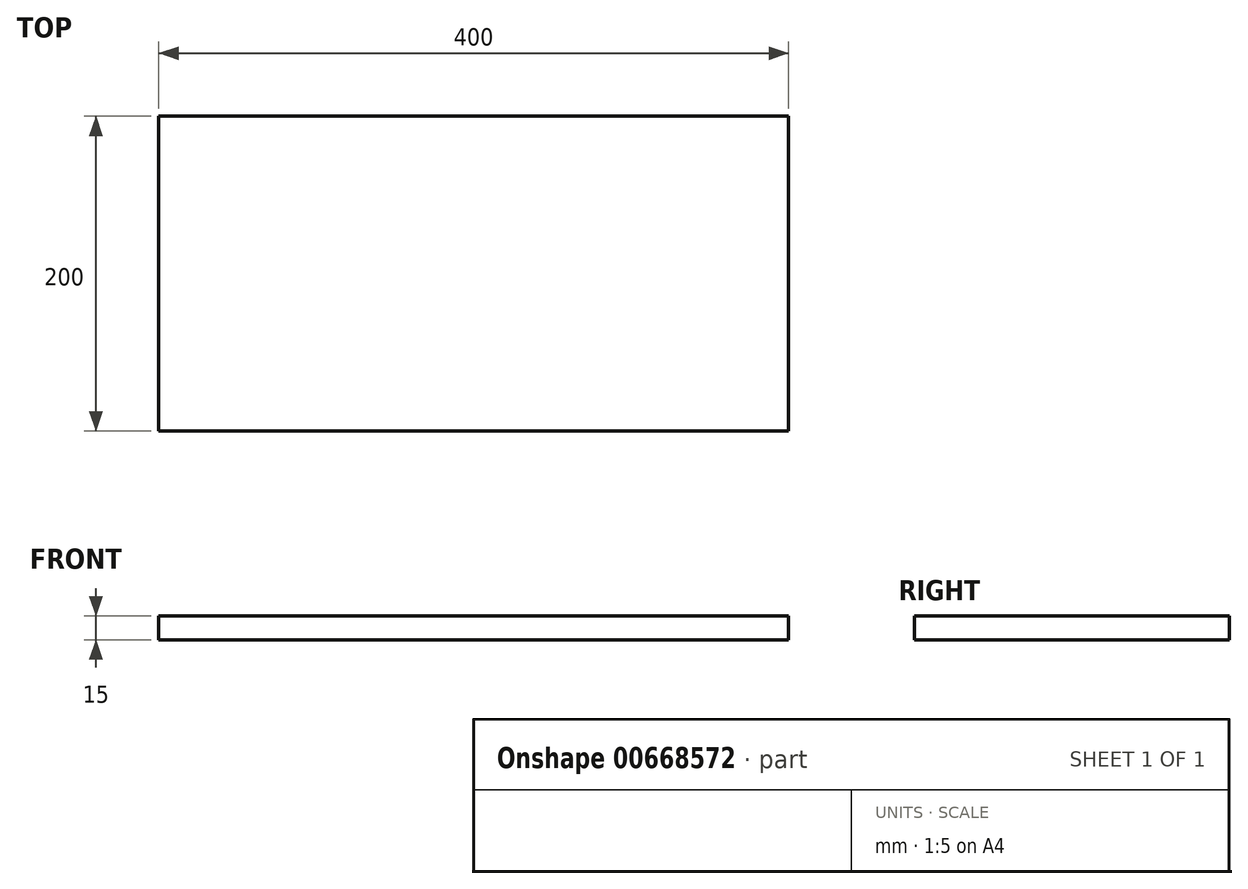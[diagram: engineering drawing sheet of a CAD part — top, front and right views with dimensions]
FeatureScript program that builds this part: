
annotation { "Feature Type Name" : "Feature", "Feature Type Description" : "" }
export const myFeature = defineFeature(function(context is Context, id is Id, definition is map)
    precondition{}
    {
        {
            var Q0;
            Q0=qCreatedBy(makeId("Top.planeOp"),FACE);
            var sketch = newSketch(context, id + "F0", { "sketchPlane" : qUnion([Q0])});
            skLineSegment(sketch, "E0.bottom", {"start": v(0, 0) * mm, "end": v(400, 0) * mm});
            skLineSegment(sketch, "E0.top", {"start": v(0, 200) * mm, "end": v(400, 200) * mm});
            skLineSegment(sketch, "E0.left", {"start": v(0, 0) * mm, "end": v(0, 200) * mm});
            skLineSegment(sketch, "E0.right", {"start": v(400, 0) * mm, "end": v(400, 200) * mm});
            skSolve(sketch);
        }
        {
            var Q0;
            Q0=makeQuery(id+"F0.imprint","IMPRINT",FACE,{"disambiguationData":[TD([[makeQuery(id+"F0.imprint","IMPRINT",EDGE,{"derivedFrom":sQuery(id+"F0.wireOp",EDGE,"E0.bottom")}),1.0]])]});
            extrude(context, id + "F1", {"entities" : qUnion([Q0]), "depth" : 15 * mm, "offsetDistance" : 25 * mm});
        }
    });
